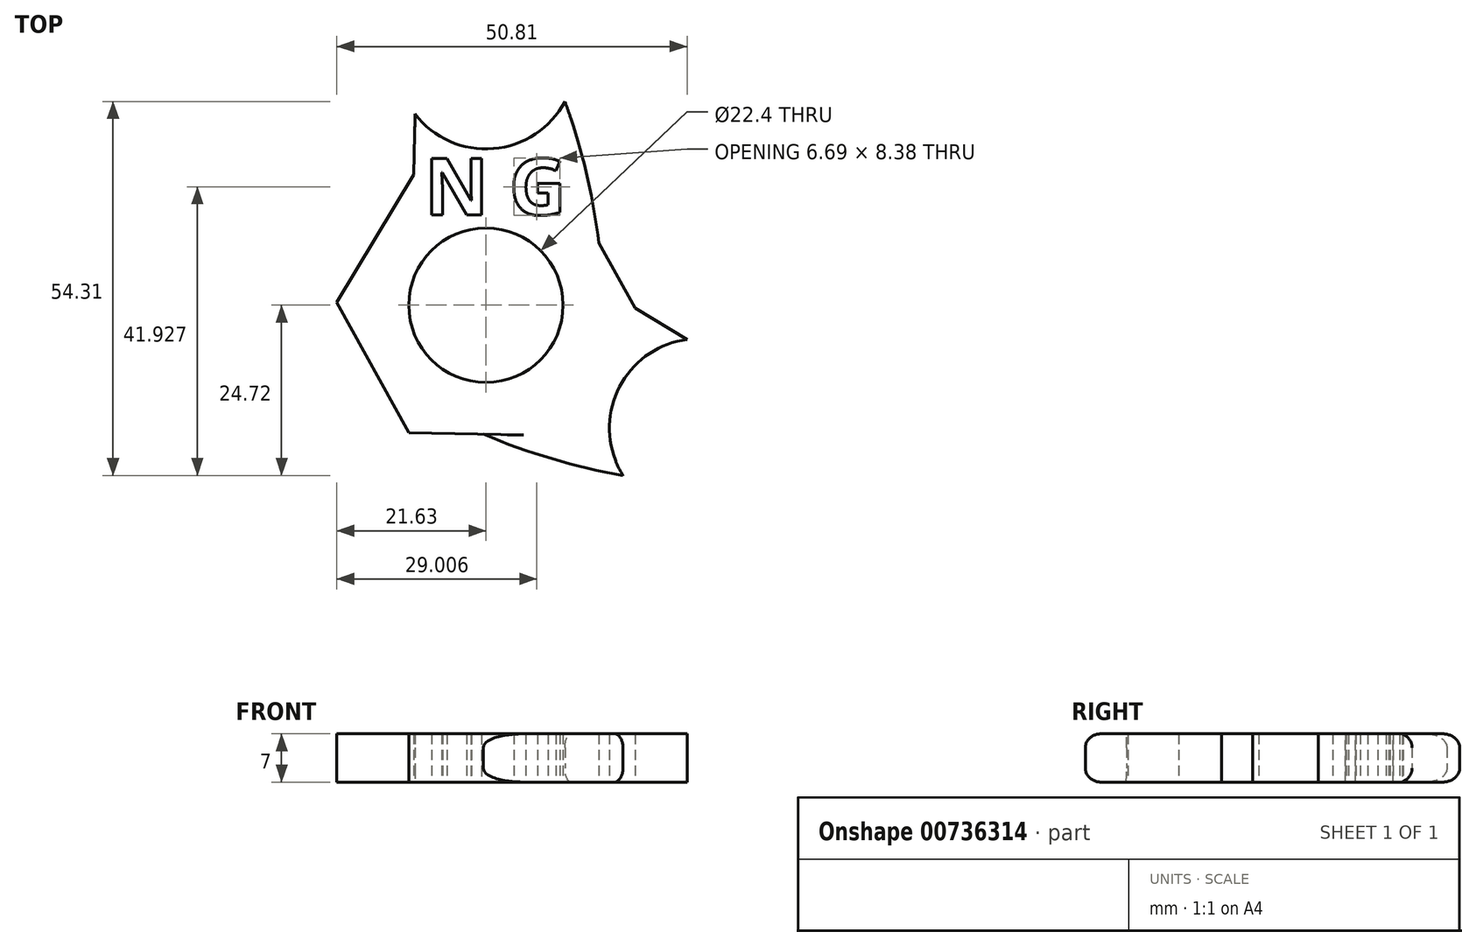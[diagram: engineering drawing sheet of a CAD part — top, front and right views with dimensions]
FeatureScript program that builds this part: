
annotation { "Feature Type Name" : "Feature", "Feature Type Description" : "" }
export const myFeature = defineFeature(function(context is Context, id is Id, definition is map)
    precondition{}
    {
        {
            var Q0;
            Q0=qCreatedBy(makeId("Top.planeOp"),FACE);
            var sketch = newSketch(context, id + "F0", { "sketchPlane" : qUnion([Q0])});
            skCircle(sketch, "E0", {"center": v(0, 0) * mm, "radius": 11.2 * mm});
            skCircle(sketch, "E1.cCircle", {"center": v(0, 0) * mm, "radius": 18.73 * mm, "construction": true});
            skLineSegment(sketch, "E1.0", {"start": v(-21.63, 0.42) * mm, "end": v(-10.45, 18.94) * mm});
            skLineSegment(sketch, "E1.1", {"start": v(-10.45, 18.94) * mm, "end": v(11.18, 18.52) * mm});
            skLineSegment(sketch, "E1.2", {"start": v(11.18, 18.52) * mm, "end": v(21.63, -0.42) * mm});
            skLineSegment(sketch, "E1.3", {"start": v(21.63, -0.42) * mm, "end": v(10.45, -18.94) * mm});
            skLineSegment(sketch, "E1.4", {"start": v(10.45, -18.94) * mm, "end": v(-11.18, -18.52) * mm});
            skLineSegment(sketch, "E1.5", {"start": v(-11.18, -18.52) * mm, "end": v(-21.63, 0.42) * mm});
            skPoint(sketch, "E1.0.midPoint", {"position": v(-16.04, 9.68) * mm});
            skCircle(sketch, "E2.cCircle", {"center": v(0, 35.66) * mm, "radius": 7.17 * mm, "construction": true});
            skLineSegment(sketch, "E2.0", {"start": v(-7.3, 39.55) * mm, "end": v(-0.29, 43.93) * mm});
            skLineSegment(sketch, "E2.1", {"start": v(-0.29, 43.93) * mm, "end": v(7.02, 40.05) * mm});
            skLineSegment(sketch, "E2.2", {"start": v(7.02, 40.05) * mm, "end": v(7.3, 31.78) * mm});
            skLineSegment(sketch, "E2.3", {"start": v(7.3, 31.78) * mm, "end": v(0.29, 27.4) * mm});
            skLineSegment(sketch, "E2.4", {"start": v(0.29, 27.4) * mm, "end": v(-7.02, 31.28) * mm});
            skLineSegment(sketch, "E2.5", {"start": v(-7.02, 31.28) * mm, "end": v(-7.3, 39.55) * mm});
            skPoint(sketch, "E2.0.midPoint", {"position": v(-3.8, 41.74) * mm});
            skLineSegment(sketch, "E3", {"start": v(-7.16, 35.41) * mm, "end": v(7.18, 35.41) * mm, "construction": true});
            skCircle(sketch, "E4", {"center": v(0, 35.66) * mm, "radius": 12.97 * mm});
            skCircle(sketch, "E5.1.1", {"center": v(-30.88, -17.83) * mm, "radius": 12.97 * mm});
            skCircle(sketch, "E5.1.2", {"center": v(-30.88, -17.83) * mm, "radius": 7.17 * mm, "construction": true});
            skLineSegment(sketch, "E5.1.10", {"start": v(-27.09, -23.9) * mm, "end": v(-34.26, -11.49) * mm, "construction": true});
            skPoint(sketch, "E5.1.11", {"position": v(-0.36, -18.73) * mm});
            skPoint(sketch, "E5.1.12", {"position": v(-34.25, -24.16) * mm});
            skLineSegment(sketch, "E5.1.13", {"start": v(-37.9, -22.22) * mm, "end": v(-38.2, -13.95) * mm});
            skLineSegment(sketch, "E5.1.14", {"start": v(-30.6, -26.1) * mm, "end": v(-37.9, -22.22) * mm});
            skLineSegment(sketch, "E5.1.15", {"start": v(-23.58, -21.72) * mm, "end": v(-30.6, -26.1) * mm});
            skLineSegment(sketch, "E5.1.16", {"start": v(-38.2, -13.95) * mm, "end": v(-31.17, -9.56) * mm});
            skLineSegment(sketch, "E5.1.17", {"start": v(-23.87, -13.45) * mm, "end": v(-23.58, -21.72) * mm});
            skLineSegment(sketch, "E5.1.18", {"start": v(-31.17, -9.56) * mm, "end": v(-23.87, -13.45) * mm});
            skCircle(sketch, "E5.2.1", {"center": v(30.88, -17.83) * mm, "radius": 12.97 * mm});
            skCircle(sketch, "E5.2.2", {"center": v(30.88, -17.83) * mm, "radius": 7.17 * mm, "construction": true});
            skLineSegment(sketch, "E5.2.10", {"start": v(34.25, -11.5) * mm, "end": v(27.08, -23.92) * mm, "construction": true});
            skPoint(sketch, "E5.2.11", {"position": v(16.4, 9.05) * mm});
            skPoint(sketch, "E5.2.12", {"position": v(38.05, -17.58) * mm});
            skLineSegment(sketch, "E5.2.13", {"start": v(38.2, -21.72) * mm, "end": v(31.17, -26.1) * mm});
            skLineSegment(sketch, "E5.2.14", {"start": v(37.9, -13.45) * mm, "end": v(38.2, -21.72) * mm});
            skLineSegment(sketch, "E5.2.15", {"start": v(30.6, -9.56) * mm, "end": v(37.9, -13.45) * mm});
            skLineSegment(sketch, "E5.2.16", {"start": v(31.17, -26.1) * mm, "end": v(23.87, -22.22) * mm});
            skLineSegment(sketch, "E5.2.17", {"start": v(23.58, -13.95) * mm, "end": v(30.6, -9.56) * mm});
            skLineSegment(sketch, "E5.2.18", {"start": v(23.87, -22.22) * mm, "end": v(23.58, -13.95) * mm});
            skArc(sketch, "E6", {"start": v(16.4, 9.05) * mm, "mid": v(14.5, 19.46) * mm, "end": v(11.46, 29.59) * mm});
            skPoint(sketch, "E6.endSnap0", {"position": v(3.8, 29.59) * mm});
            skLineSegment(sketch, "E7", {"start": v(21.63, -0.42) * mm, "end": v(29.18, -4.97) * mm});
            skPoint(sketch, "E8.1.1", {"position": v(-27.52, -11.5) * mm});
            skLineSegment(sketch, "E8.1.11", {"start": v(-10.45, 18.94) * mm, "end": v(-10.28, 27.75) * mm});
            skArc(sketch, "E8.1.17", {"start": v(-16.04, 9.68) * mm, "mid": v(-24.1, 2.83) * mm, "end": v(-31.35, -4.87) * mm});
            skPoint(sketch, "E8.2.1", {"position": v(23.72, -18.08) * mm});
            skLineSegment(sketch, "E8.2.11", {"start": v(-11.18, -18.52) * mm, "end": v(-18.9, -22.78) * mm});
            skArc(sketch, "E8.2.13", {"start": v(19.9, -24.72) * mm, "mid": v(42.63, -23.35) * mm, "end": v(29.18, -4.97) * mm});
            skArc(sketch, "E8.2.17", {"start": v(-0.36, -18.73) * mm, "mid": v(9.6, -22.29) * mm, "end": v(19.9, -24.72) * mm});
            skText(sketch, "E9", { "text": "N G", "fontName": "OpenSans-Bold.ttf"});
            skArc(sketch, "E10.1.21", {"start": v(11.46, 29.59) * mm, "mid": v(-1.09, 48.6) * mm, "end": v(-10.28, 27.75) * mm});
            skArc(sketch, "E10.2.21", {"start": v(-31.35, -4.87) * mm, "mid": v(-41.54, -25.24) * mm, "end": v(-18.9, -22.78) * mm});
            const initialGuessF0  = {"E9": [-0.00888, 0.01313, 1, 0, 0.00822]};
            skSetInitialGuess(sketch, initialGuessF0);
            skSolve(sketch);
        }
        {
            var Q0;
            Q0=makeQuery(id+"F0.imprint","IMPRINT",FACE,{"disambiguationData":[TD([[makeQuery(id+"F0.imprint","IMPRINT",EDGE,{"derivedFrom":sQuery(id+"F0.wireOp",EDGE,"E2.0")}),1.0]])]});
            var Q1;
            {var subQ4=sQuery(id+"F0.wireOp",EDGE,"E9.sketch_text.stroke-9");Q1=makeQuery(id+"F0.imprint","IMPRINT",FACE,{"disambiguationData":[TD([[makeQuery(id+"F0.imprint","IMPRINT",EDGE,{"derivedFrom":subQ4}),1.0]])]});}
            var Q2;
            {var subQ23=sQuery(id+"F0.wireOp",EDGE,"E9.sketch_text.stroke-0");Q2=makeQuery(id+"F0.imprint","IMPRINT",FACE,{"disambiguationData":[TD([[makeQuery(id+"F0.imprint","IMPRINT",EDGE,{"derivedFrom":subQ23}),1.0]])]});}
            var Q3;
            {var subQ10=sQuery(id+"F0.wireOp",EDGE,"E9.sketch_text.stroke-7");Q3=makeQuery(id+"F0.imprint","IMPRINT",FACE,{"disambiguationData":[TD([[makeQuery(id+"F0.imprint","IMPRINT",EDGE,{"derivedFrom":subQ10}),1.0]])]});}
            var Q4;
            {var subQ3=sQuery(id+"F0.wireOp",EDGE,"E8.1.17");Q4=makeQuery(id+"F0.imprint","IMPRINT",FACE,{"disambiguationData":[TD([[makeQuery(id+"F0.imprint","IMPRINT",EDGE,{"derivedFrom":subQ3}),1.0]])]});}
            var Q5;
            {var subQ1=sQuery(id+"F0.wireOp",EDGE,"E8.2.17");Q5=makeQuery(id+"F0.imprint","IMPRINT",FACE,{"disambiguationData":[TD([[makeQuery(id+"F0.imprint","IMPRINT",EDGE,{"derivedFrom":subQ1}),1.0]])]});}
            var Q6;
            Q6=makeQuery(id+"F0.imprint","IMPRINT",FACE,{"disambiguationData":[TD([[makeQuery(id+"F0.imprint","IMPRINT",EDGE,{"derivedFrom":sQuery(id+"F0.wireOp",EDGE,"E5.1.18")}),1.0]])]});
            var Q7;
            {var subQ0=sQuery(id+"F0.wireOp",EDGE,"E9.sketch_text.stroke-2");Q7=makeQuery(id+"F0.imprint","IMPRINT",FACE,{"disambiguationData":[TD([[makeQuery(id+"F0.imprint","IMPRINT",EDGE,{"derivedFrom":subQ0}),1.0]])]});}
            var Q8;
            Q8=makeQuery(id+"F0.imprint","IMPRINT",FACE,{"disambiguationData":[TD([[makeQuery(id+"F0.imprint","IMPRINT",EDGE,{"derivedFrom":sQuery(id+"F0.wireOp",EDGE,"E5.2.18")}),1.0]])]});
            extrude(context, id + "F1", {"entities" : qUnion([Q0, Q1, Q2, Q3, Q4, Q5, Q6, Q7, Q8]), "depth" : 7 * mm, "offsetDistance" : 25 * mm});
        }
        {
            var Q0;
            Q0=makeQuery(id+"F1.opExtrude","CAP_EDGE",EDGE,{"disambiguationData":[OSD([sQuery(id+"F0.wireOp",EDGE,"E4")])],"isStart":false});
            var Q1;
            Q1=makeQuery(id+"F1.opExtrude","CAP_EDGE",EDGE,{"disambiguationData":[OSD([sQuery(id+"F0.wireOp",EDGE,"E6")])],"isStart":false});
            var Q2;
            Q2=makeQuery(id+"F1.opExtrude","CAP_EDGE",EDGE,{"disambiguationData":[OSD([sQuery(id+"F0.wireOp",EDGE,"E1.2")])],"isStart":false});
            var Q3;
            Q3=makeQuery(id+"F1.opExtrude","CAP_EDGE",EDGE,{"disambiguationData":[OSD([sQuery(id+"F0.wireOp",EDGE,"E7")])],"isStart":false});
            var Q4;
            Q4=makeQuery(id+"F1.opExtrude","CAP_EDGE",EDGE,{"disambiguationData":[OSD([sQuery(id+"F0.wireOp",EDGE,"E5.2.1")])],"isStart":false});
            var Q5;
            Q5=makeQuery(id+"F1.opExtrude","CAP_EDGE",EDGE,{"disambiguationData":[OSD([sQuery(id+"F0.wireOp",EDGE,"E8.2.17")])],"isStart":false});
            var Q6;
            Q6=makeQuery(id+"F1.opExtrude","CAP_EDGE",EDGE,{"disambiguationData":[OSD([sQuery(id+"F0.wireOp",EDGE,"E1.4")])],"isStart":false});
            var Q7;
            Q7=makeQuery(id+"F1.opExtrude","CAP_EDGE",EDGE,{"disambiguationData":[OSD([sQuery(id+"F0.wireOp",EDGE,"E8.2.11")])],"isStart":false});
            var Q8;
            Q8=makeQuery(id+"F1.opExtrude","CAP_EDGE",EDGE,{"disambiguationData":[OSD([sQuery(id+"F0.wireOp",EDGE,"E5.1.1")])],"isStart":false});
            var Q9;
            Q9=makeQuery(id+"F1.opExtrude","CAP_EDGE",EDGE,{"disambiguationData":[OSD([sQuery(id+"F0.wireOp",EDGE,"E8.1.17")])],"isStart":false});
            var Q10;
            Q10=makeQuery(id+"F1.opExtrude","CAP_EDGE",EDGE,{"disambiguationData":[OSD([sQuery(id+"F0.wireOp",EDGE,"E1.0")])],"isStart":false});
            var Q11;
            Q11=makeQuery(id+"F1.opExtrude","CAP_EDGE",EDGE,{"disambiguationData":[OSD([sQuery(id+"F0.wireOp",EDGE,"E8.1.11")])],"isStart":false});
            fillet(context, id + "F2", {"entities" : qUnion([Q0, Q1, Q2, Q3, Q4, Q5, Q6, Q7, Q8, Q9, Q10, Q11]), "radius" : 2 * mm, "tangentPropagation" : true, "allowEdgeOverflow" : false});
        }
        {
            var Q0;
            Q0=makeQuery(id+"F1.opExtrude","CAP_EDGE",EDGE,{"disambiguationData":[OSD([sQuery(id+"F0.wireOp",EDGE,"E5.1.1")])],"isStart":true});
            var Q1;
            Q1=makeQuery(id+"F1.opExtrude","CAP_EDGE",EDGE,{"disambiguationData":[OSD([sQuery(id+"F0.wireOp",EDGE,"E8.2.11")])],"isStart":true});
            var Q2;
            Q2=makeQuery(id+"F1.opExtrude","CAP_EDGE",EDGE,{"disambiguationData":[OSD([sQuery(id+"F0.wireOp",EDGE,"E1.4")])],"isStart":true});
            var Q3;
            Q3=makeQuery(id+"F1.opExtrude","CAP_EDGE",EDGE,{"disambiguationData":[OSD([sQuery(id+"F0.wireOp",EDGE,"E8.2.17")])],"isStart":true});
            var Q4;
            Q4=makeQuery(id+"F1.opExtrude","CAP_EDGE",EDGE,{"disambiguationData":[OSD([sQuery(id+"F0.wireOp",EDGE,"E5.2.1")])],"isStart":true});
            var Q5;
            Q5=makeQuery(id+"F1.opExtrude","CAP_EDGE",EDGE,{"disambiguationData":[OSD([sQuery(id+"F0.wireOp",EDGE,"E7")])],"isStart":true});
            var Q6;
            Q6=makeQuery(id+"F1.opExtrude","CAP_EDGE",EDGE,{"disambiguationData":[OSD([sQuery(id+"F0.wireOp",EDGE,"E1.2")])],"isStart":true});
            var Q7;
            Q7=makeQuery(id+"F1.opExtrude","CAP_EDGE",EDGE,{"disambiguationData":[OSD([sQuery(id+"F0.wireOp",EDGE,"E6")])],"isStart":true});
            var Q8;
            Q8=makeQuery(id+"F1.opExtrude","CAP_EDGE",EDGE,{"disambiguationData":[OSD([sQuery(id+"F0.wireOp",EDGE,"E4")])],"isStart":true});
            var Q9;
            Q9=makeQuery(id+"F1.opExtrude","CAP_EDGE",EDGE,{"disambiguationData":[OSD([sQuery(id+"F0.wireOp",EDGE,"E8.1.11")])],"isStart":true});
            var Q10;
            Q10=makeQuery(id+"F1.opExtrude","CAP_EDGE",EDGE,{"disambiguationData":[OSD([sQuery(id+"F0.wireOp",EDGE,"E1.0")])],"isStart":true});
            var Q11;
            Q11=makeQuery(id+"F1.opExtrude","CAP_EDGE",EDGE,{"disambiguationData":[OSD([sQuery(id+"F0.wireOp",EDGE,"E8.1.17")])],"isStart":true});
            fillet(context, id + "F3", {"entities" : qUnion([Q0, Q1, Q2, Q3, Q4, Q5, Q6, Q7, Q8, Q9, Q10, Q11]), "radius" : 2 * mm, "tangentPropagation" : true, "allowEdgeOverflow" : false});
        }
    });
